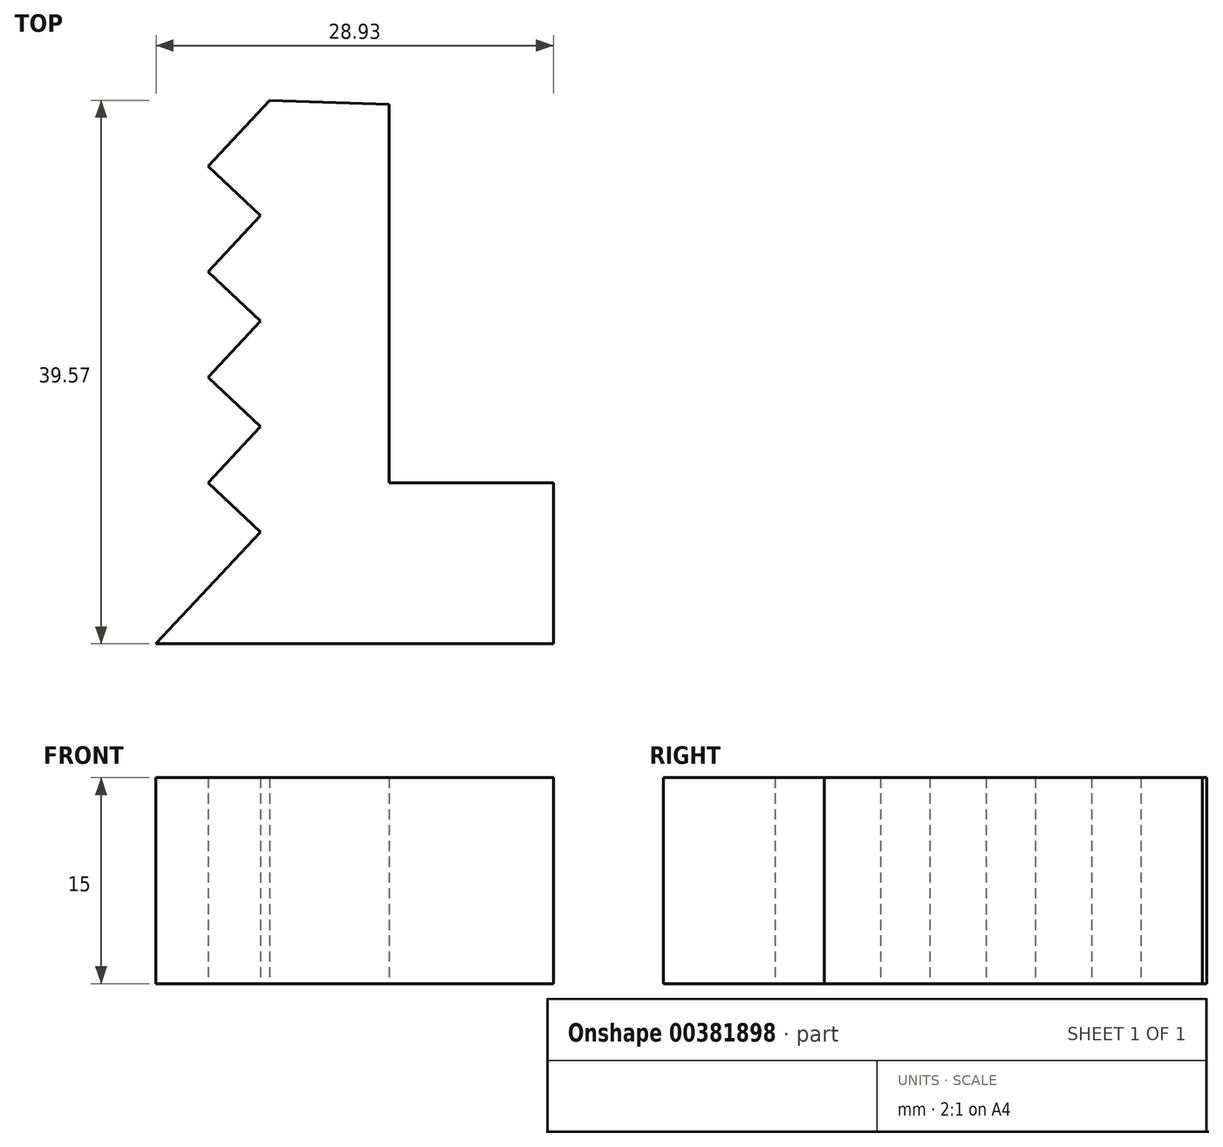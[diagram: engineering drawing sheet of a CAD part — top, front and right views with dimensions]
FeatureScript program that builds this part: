
annotation { "Feature Type Name" : "Feature", "Feature Type Description" : "" }
export const myFeature = defineFeature(function(context is Context, id is Id, definition is map)
    precondition{}
    {
        {
            var Q0;
            Q0=qCreatedBy(makeId("Top.planeOp"),FACE);
            var sketch = newSketch(context, id + "F0", { "sketchPlane" : qUnion([Q0])});
            skLineSegment(sketch, "E0", {"start": v(-43.42, 54.2) * mm, "end": v(-47.9, 49.4) * mm});
            skLineSegment(sketch, "E1", {"start": v(-47.9, 49.4) * mm, "end": v(-44.07, 45.81) * mm});
            skLineSegment(sketch, "E2", {"start": v(-44.07, 45.81) * mm, "end": v(-47.9, 41.72) * mm});
            skLineSegment(sketch, "E3", {"start": v(-47.9, 41.72) * mm, "end": v(-44.07, 38.13) * mm});
            skLineSegment(sketch, "E4", {"start": v(-44.07, 38.13) * mm, "end": v(-47.9, 34.04) * mm});
            skLineSegment(sketch, "E5", {"start": v(-47.9, 34.04) * mm, "end": v(-44.07, 30.44) * mm});
            skLineSegment(sketch, "E6", {"start": v(-44.07, 30.44) * mm, "end": v(-47.9, 26.35) * mm});
            skLineSegment(sketch, "E7", {"start": v(-47.9, 26.35) * mm, "end": v(-44.07, 22.75) * mm});
            skLineSegment(sketch, "E8", {"start": v(-44.07, 22.75) * mm, "end": v(-51.7, 14.63) * mm});
            skLineSegment(sketch, "E9", {"start": v(-51.7, 14.63) * mm, "end": v(-22.76, 14.63) * mm});
            skLineSegment(sketch, "E10", {"start": v(-22.76, 14.63) * mm, "end": v(-22.76, 26.35) * mm});
            skLineSegment(sketch, "E11", {"start": v(-22.76, 26.35) * mm, "end": v(-34.73, 26.35) * mm});
            skLineSegment(sketch, "E12", {"start": v(-34.73, 26.35) * mm, "end": v(-34.73, 53.9) * mm});
            skLineSegment(sketch, "E13", {"start": v(-34.73, 53.9) * mm, "end": v(-43.42, 54.2) * mm});
            skSolve(sketch);
        }
        {
            var Q0;
            Q0 = qSketchRegion(id + "F0", true);
            extrude(context, id + "F1", {"entities" : qUnion([Q0]), "depth" : 15 * mm});
        }
    });
